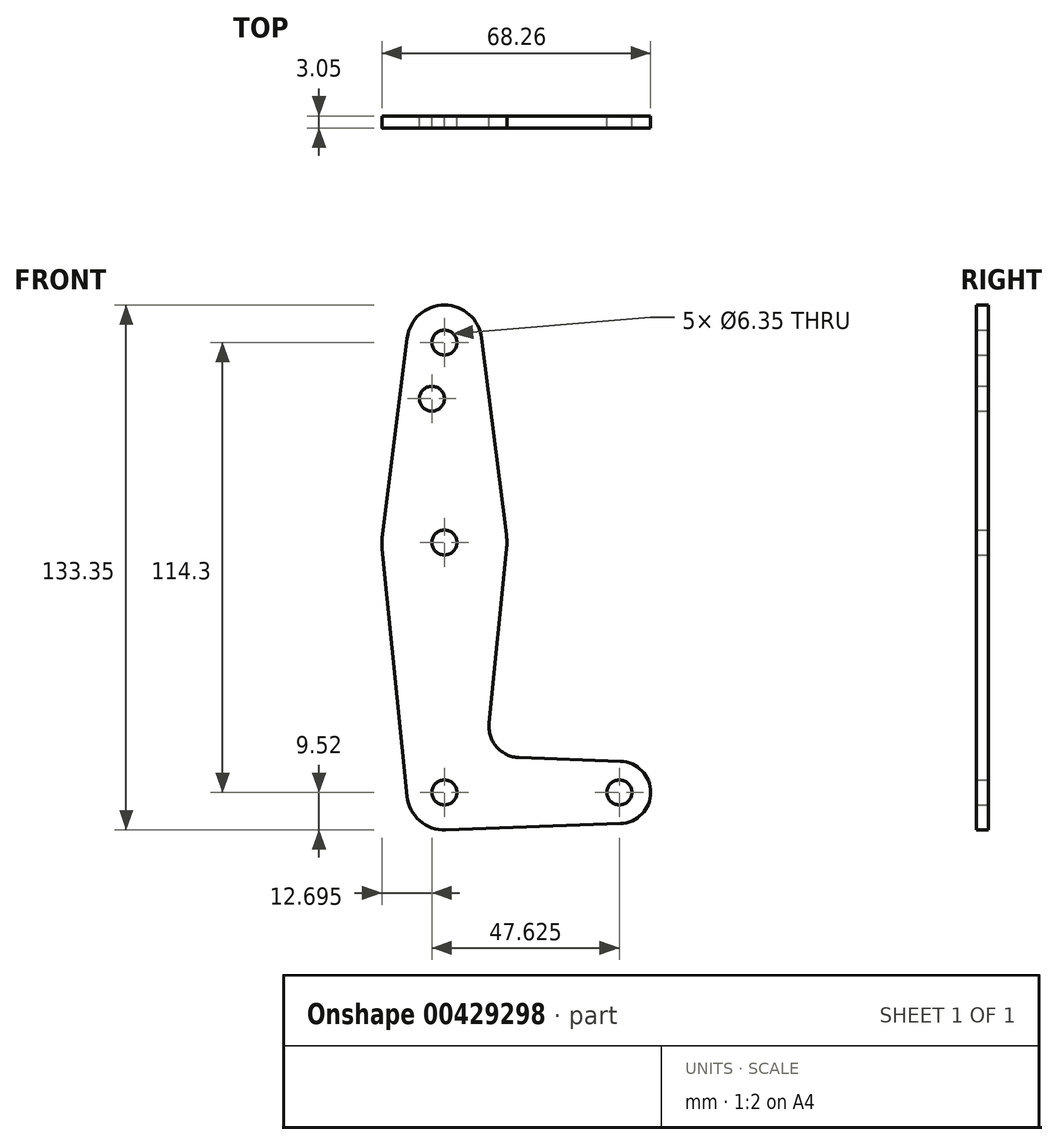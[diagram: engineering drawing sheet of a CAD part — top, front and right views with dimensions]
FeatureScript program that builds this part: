
annotation { "Feature Type Name" : "Feature", "Feature Type Description" : "" }
export const myFeature = defineFeature(function(context is Context, id is Id, definition is map)
    precondition{}
    {
        {
            var Q0;
            Q0=qCreatedBy(makeId("Front.planeOp"),FACE);
            var sketch = newSketch(context, id + "F0", { "sketchPlane" : qUnion([Q0])});
            skLineSegment(sketch, "E0", {"start": v(0, 114.3) * mm, "end": v(0, 63.5) * mm, "construction": true});
            skLineSegment(sketch, "E1", {"start": v(0, 63.5) * mm, "end": v(0, 0) * mm, "construction": true});
            skLineSegment(sketch, "E2", {"start": v(0, 0) * mm, "end": v(44.45, 0) * mm, "construction": true});
            skCircle(sketch, "E3", {"center": v(-3.18, 100.03) * mm, "radius": 3.18 * mm});
            skCircle(sketch, "E4", {"center": v(0, 114.3) * mm, "radius": 9.53 * mm});
            skCircle(sketch, "E5", {"center": v(0, 63.5) * mm, "radius": 15.88 * mm});
            skCircle(sketch, "E6", {"center": v(0, 0) * mm, "radius": 9.53 * mm});
            skCircle(sketch, "E7", {"center": v(44.45, 0) * mm, "radius": 7.94 * mm});
            skCircle(sketch, "E8", {"center": v(0, 114.3) * mm, "radius": 3.18 * mm});
            skCircle(sketch, "E9", {"center": v(0, 63.5) * mm, "radius": 3.18 * mm});
            skCircle(sketch, "E10", {"center": v(0, 0) * mm, "radius": 3.18 * mm});
            skCircle(sketch, "E11", {"center": v(44.45, 0) * mm, "radius": 3.18 * mm});
            skLineSegment(sketch, "E12", {"start": v(-9.45, 115.5) * mm, "end": v(-15.75, 65.48) * mm});
            skLineSegment(sketch, "E13", {"start": v(9.45, 115.5) * mm, "end": v(15.75, 65.48) * mm});
            skLineSegment(sketch, "E14", {"start": v(-15.8, 61.91) * mm, "end": v(-9.48, -0.95) * mm});
            skLineSegment(sketch, "E15", {"start": v(15.8, 61.91) * mm, "end": v(11.34, 17.6) * mm});
            skLineSegment(sketch, "E16", {"start": v(18.97, 8.85) * mm, "end": v(44.73, 7.93) * mm});
            skLineSegment(sketch, "E17", {"start": v(0.34, -9.52) * mm, "end": v(44.73, -7.93) * mm});
            skArc(sketch, "E18.filletArc", {"start": v(11.34, 17.6) * mm, "mid": v(13.26, 11.57) * mm, "end": v(18.97, 8.85) * mm});
            skSolve(sketch);
        }
        {
            var Q0;
            Q0 = qSketchRegion(id + "F0", true);
            extrude(context, id + "F1", {"entities" : qUnion([Q0]), "depth" : 3.05 * mm});
        }
    });
